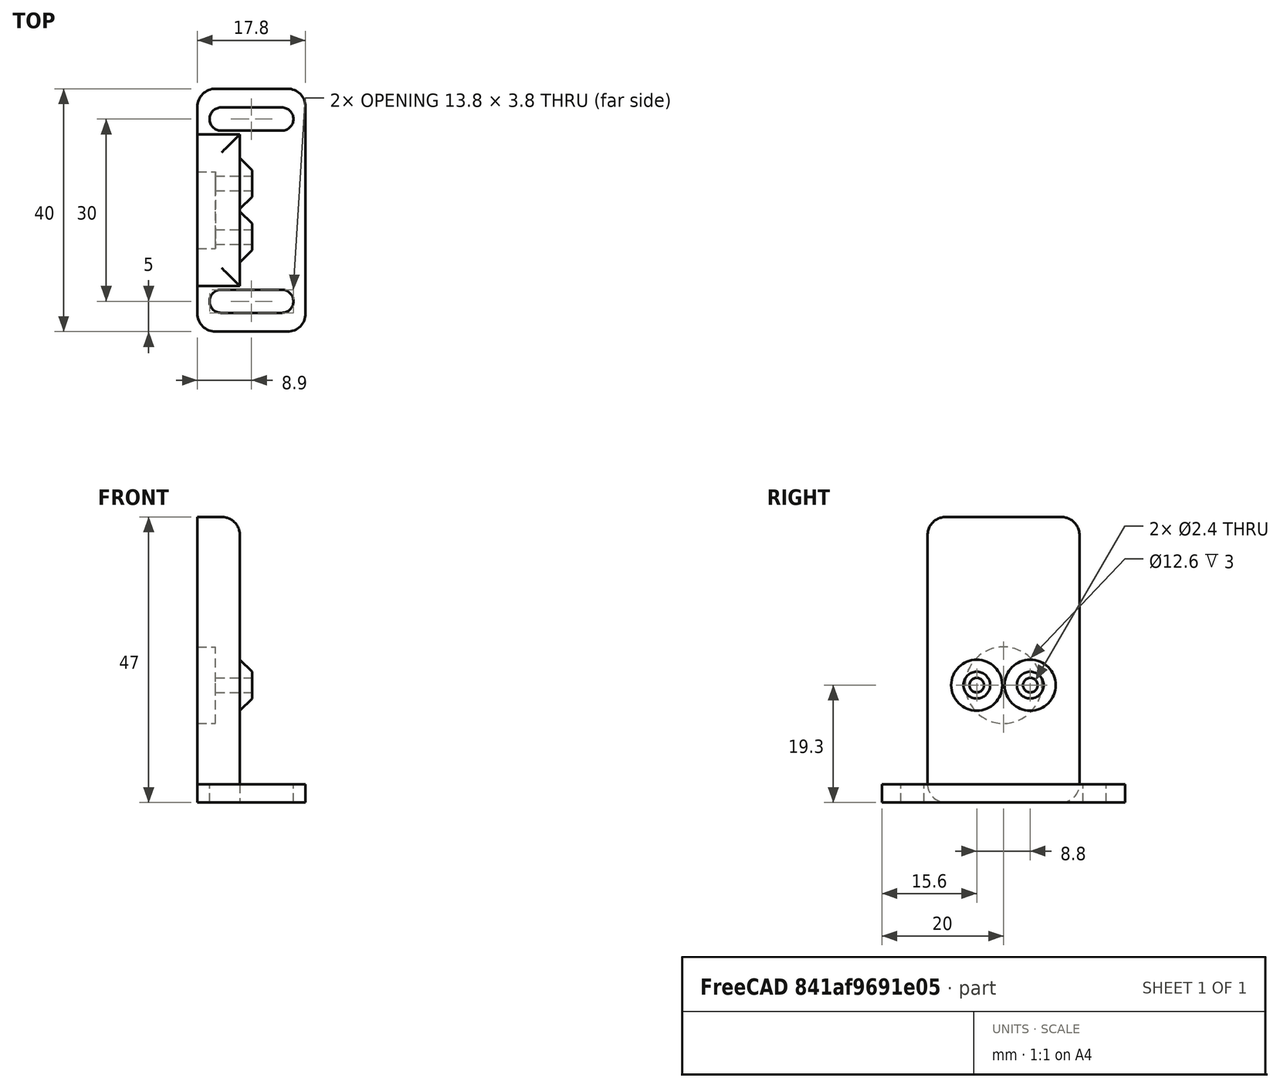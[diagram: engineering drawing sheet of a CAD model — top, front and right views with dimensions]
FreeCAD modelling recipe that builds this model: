
FCSTD DOCUMENT  (FreeCAD 0.18.4R)
Label: photo_resistor
License: FreeArt
LicenseURL: http://artlibre.org/licence/lal
objects: Part::Cylinder×2, Part::FeaturePython×2, Part::MultiFuse×2, Part::Compound×2, Spreadsheet::Sheet×1, Part::Box×1, Part::Fillet×1, Part::Cone×1, Part::Cut×1, Part::Feature×1
note: 13 computed .brp shape members not serialized (recipe doc carries the construction recipe); baked Part::Feature solids carry a one-line shape summary decoded from their .brp

FEATURE [Spreadsheet::Sheet] Spreadsheet  label="p"
  cells = A1=resistor_r; B1(resistor_r)=6.3; A2=resistor_z; B2(resistor_z)=3; A3=resistor_wire_r; B3(resistor_wire_r)=1.2; A4=resistor_wire_dist; B4(resistor_wire_dist)=8.800000000000001; A5=side_wall; B5(side_wall)=4; A6=bottom_wall; B6(bottom_wall)=2; A7=window_wall_y; B7(window_wall_y)=25; A8=window_wall_z; B8(window_wall_z)=45; A9=wire_cone_size; B9(wire_cone_size)=3; A10=wire_cone_min_border; B10(wire_cone_min_border)=1; A11=wire_cone_max_border; B11(wire_cone_max_border)=4; A12=cuvette_window_z_off; B12(cuvette_window_z_off)=10; A13=cuvette_window_z_off_extra; B13(cuvette_window_z_off_extra)=1
FEATURE [Part::Box] Box009  label="cuvetter window wall"
  AttacherType = Attacher::AttachEngine3D
  Height = 47
  Length = 7
  Width = 25
  expr: Length = p.side_wall + p.resistor_z
  expr: Height = p.window_wall_z + p.bottom_wall
  expr: Width = p.window_wall_y
FEATURE [Part::Fillet] Fillet  label="cuvetter window wall fillet"
  Base = -> Box009
  Edges = 5 edges r=3: [Edge6,Edge9,Edge10,Edge11,Edge12]
FEATURE [Part::Cylinder] Cylinder002  label="resistor body"
  Angle = 360
  AttacherType = Attacher::AttachEngine3D
  Height = 3
  Radius = 6.3
  expr: Height = p.resistor_z
  expr: Radius = p.resistor_r
FEATURE [Part::Cylinder] Cylinder003  label="resistor wire hole"
  Angle = 360
  AttacherType = Attacher::AttachEngine3D
  Height = 30
  Radius = 1.2
  expr: Radius = p.resistor_wire_r
FEATURE [Part::FeaturePython] Array  label="resistor wire hole array"  # Draft array (typed FeaturePython)
  Angle = 360
  ArrayType = 0
  Axis = (0,0,1)
  Base = -> Cylinder003
  Center = (0,0,0)
  Fuse = false
  IntervalAxis = (0,0,0)
  IntervalX = (1,0,0)
  IntervalY = (0,8.8,0)
  IntervalZ = (0,0,1)
  NumberPolar = 1
  NumberX = 1
  NumberY = 2
  NumberZ = 1
  Placement = pos=(0,-4.4,-4) rot=(0,0,1;0rad)
  expr: Placement.Base.y = -p.resistor_wire_dist / 2
  expr: IntervalY.y = p.resistor_wire_dist
FEATURE [Part::MultiFuse] Fusion  label="resistor extraction fusion"
  Placement = pos=(0,12.5,19.3) rot=(0,1,0;1.5708rad)
  Shapes = -> [Cylinder002,Array]
  expr: Placement.Base.z = p.bottom_wall + p.cuvette_window_z_off + p.cuvette_window_z_off_extra + p.resistor_r
  expr: Placement.Base.y = p.window_wall_y / 2
FEATURE [Part::Cone] Cone  label="resistor wire stand"
  Angle = 360
  AttacherType = Attacher::AttachEngine3D
  Height = 3
  Radius1 = 5.2
  Radius2 = 2.2
  expr: Height = p.wire_cone_size
  expr: Radius2 = p.resistor_wire_r + p.wire_cone_min_border
  expr: Radius1 = p.resistor_wire_r + p.wire_cone_max_border
FEATURE [Part::FeaturePython] Array001  label="resistor wire hole array001"  # Draft array (typed FeaturePython)
  Angle = 360
  ArrayType = 0
  Axis = (0,0,1)
  Base = -> Cone
  Center = (0,0,0)
  Fuse = false
  IntervalAxis = (0,0,0)
  IntervalX = (1,0,0)
  IntervalY = (0,8.8,0)
  IntervalZ = (0,0,1)
  NumberPolar = 1
  NumberX = 1
  NumberY = 2
  NumberZ = 1
  Placement = pos=(0,-4.4,-4) rot=(0,0,1;0rad)
  expr: Placement.Base.y = -p.resistor_wire_dist / 2
  expr: IntervalY.y = p.resistor_wire_dist
FEATURE [Part::Compound] Compound001  label="cone compound"
  Links = -> [Array001]
  Placement = pos=(10,12.5,19.3) rot=(0,1,0;1.5708rad)
  expr: Placement.Base.z = p.bottom_wall + p.cuvette_window_z_off + p.cuvette_window_z_off_extra + p.resistor_r
  expr: Placement.Base.x = p.resistor_z + p.side_wall + p.wire_cone_size
  expr: Placement.Base.y = p.window_wall_y / 2
FEATURE [Part::MultiFuse] Fusion001  label="wall fusion"
  Shapes = -> [Compound001,Fillet]
FEATURE [Part::Cut] Cut  label="wall resistor cut"
  Base = -> Fusion001
  Placement = pos=(-2.4,0,0) rot=(0,0,1;0rad)
  Tool = -> Fusion
FEATURE [Part::Feature] Cut002001  label="attach plane y dir"
  shape: bbox 17.8 x 40 x 3 mm, 18 faces (baked)
FEATURE [Part::Compound] Compound  label="photo resistor compound"
  Links = -> [Cut,Cut002001]
